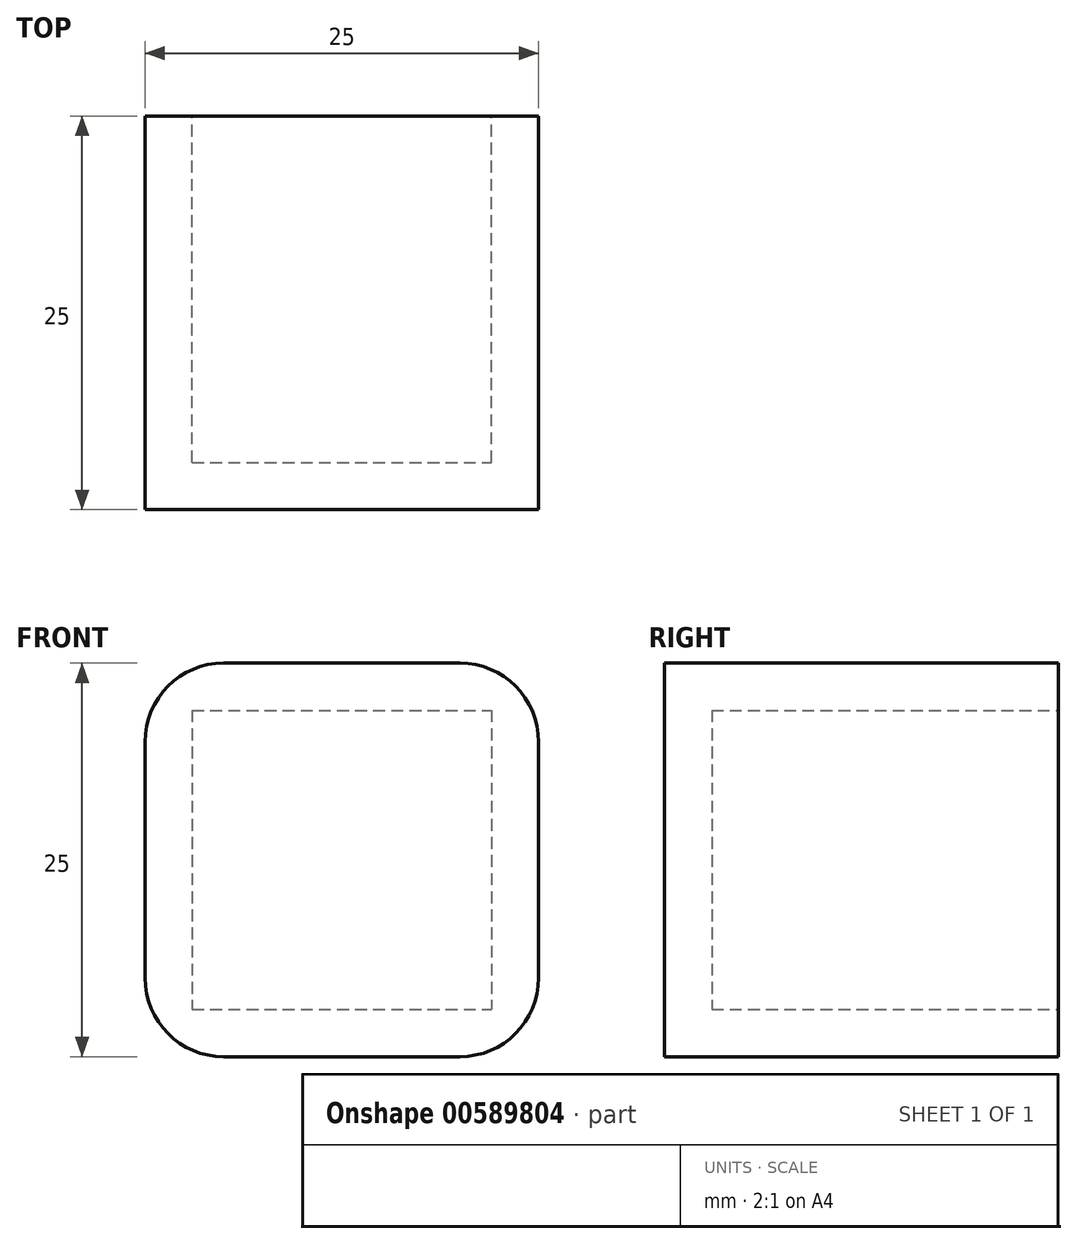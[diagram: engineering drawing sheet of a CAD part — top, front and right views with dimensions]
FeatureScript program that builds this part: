
annotation { "Feature Type Name" : "Feature", "Feature Type Description" : "" }
export const myFeature = defineFeature(function(context is Context, id is Id, definition is map)
    precondition{}
    {
        {
            var Q0;
            Q0=qCreatedBy(makeId("Top.planeOp"),FACE);
            var sketch = newSketch(context, id + "F0", { "sketchPlane" : qUnion([Q0])});
            skLineSegment(sketch, "E0.bottom", {"start": v(0, 0) * mm, "end": v(25, 0) * mm});
            skLineSegment(sketch, "E0.top", {"start": v(0, 25) * mm, "end": v(25, 25) * mm});
            skLineSegment(sketch, "E0.left", {"start": v(0, 0) * mm, "end": v(0, 25) * mm});
            skLineSegment(sketch, "E0.right", {"start": v(25, 0) * mm, "end": v(25, 25) * mm});
            skSolve(sketch);
        }
        {
            var Q0;
            Q0=makeQuery(id+"F0.imprint","IMPRINT",FACE,{"disambiguationData":[TD([[makeQuery(id+"F0.imprint","IMPRINT",EDGE,{"derivedFrom":sQuery(id+"F0.wireOp",EDGE,"E0.bottom")}),1.0]])]});
            extrude(context, id + "F1", {"entities" : qUnion([Q0]), "depth" : 25 * mm, "offsetDistance" : 25 * mm});
        }
        {
            var Q0;
            Q0=makeQuery(id+"F1.opExtrude","SWEPT_FACE",FACE,{"disambiguationData":[OSD([sQuery(id+"F0.wireOp",EDGE,"E0.top")])]});
            shell(context, id + "F2", {"entities" : qUnion([Q0]), "thickness" : 3 * mm});
        }
        {
            var Q0;
            Q0=makeQuery(id+"F1.opExtrude","CAP_EDGE",EDGE,{"disambiguationData":[OSD([sQuery(id+"F0.wireOp",EDGE,"E0.right")])],"isStart":false});
            fillet(context, id + "F3", {"entities" : qUnion([Q0]), "radius" : 5 * mm, "tangentPropagation" : true, "allowEdgeOverflow" : false});
        }
        {
            var Q0;
            Q0=makeQuery(id+"F1.opExtrude","CAP_EDGE",EDGE,{"disambiguationData":[OSD([sQuery(id+"F0.wireOp",EDGE,"E0.left")])],"isStart":false});
            fillet(context, id + "F4", {"entities" : qUnion([Q0]), "radius" : 5 * mm, "tangentPropagation" : true, "allowEdgeOverflow" : false});
        }
        {
            var Q0;
            Q0=makeQuery(id+"F1.opExtrude","CAP_EDGE",EDGE,{"disambiguationData":[OSD([sQuery(id+"F0.wireOp",EDGE,"E0.left")])],"isStart":true});
            fillet(context, id + "F5", {"entities" : qUnion([Q0]), "radius" : 5 * mm, "tangentPropagation" : true, "allowEdgeOverflow" : false});
        }
        {
            var Q0;
            Q0=makeQuery(id+"F1.opExtrude","CAP_EDGE",EDGE,{"disambiguationData":[OSD([sQuery(id+"F0.wireOp",EDGE,"E0.right")])],"isStart":true});
            fillet(context, id + "F6", {"entities" : qUnion([Q0]), "radius" : 5 * mm, "tangentPropagation" : true, "allowEdgeOverflow" : false});
        }
    });
